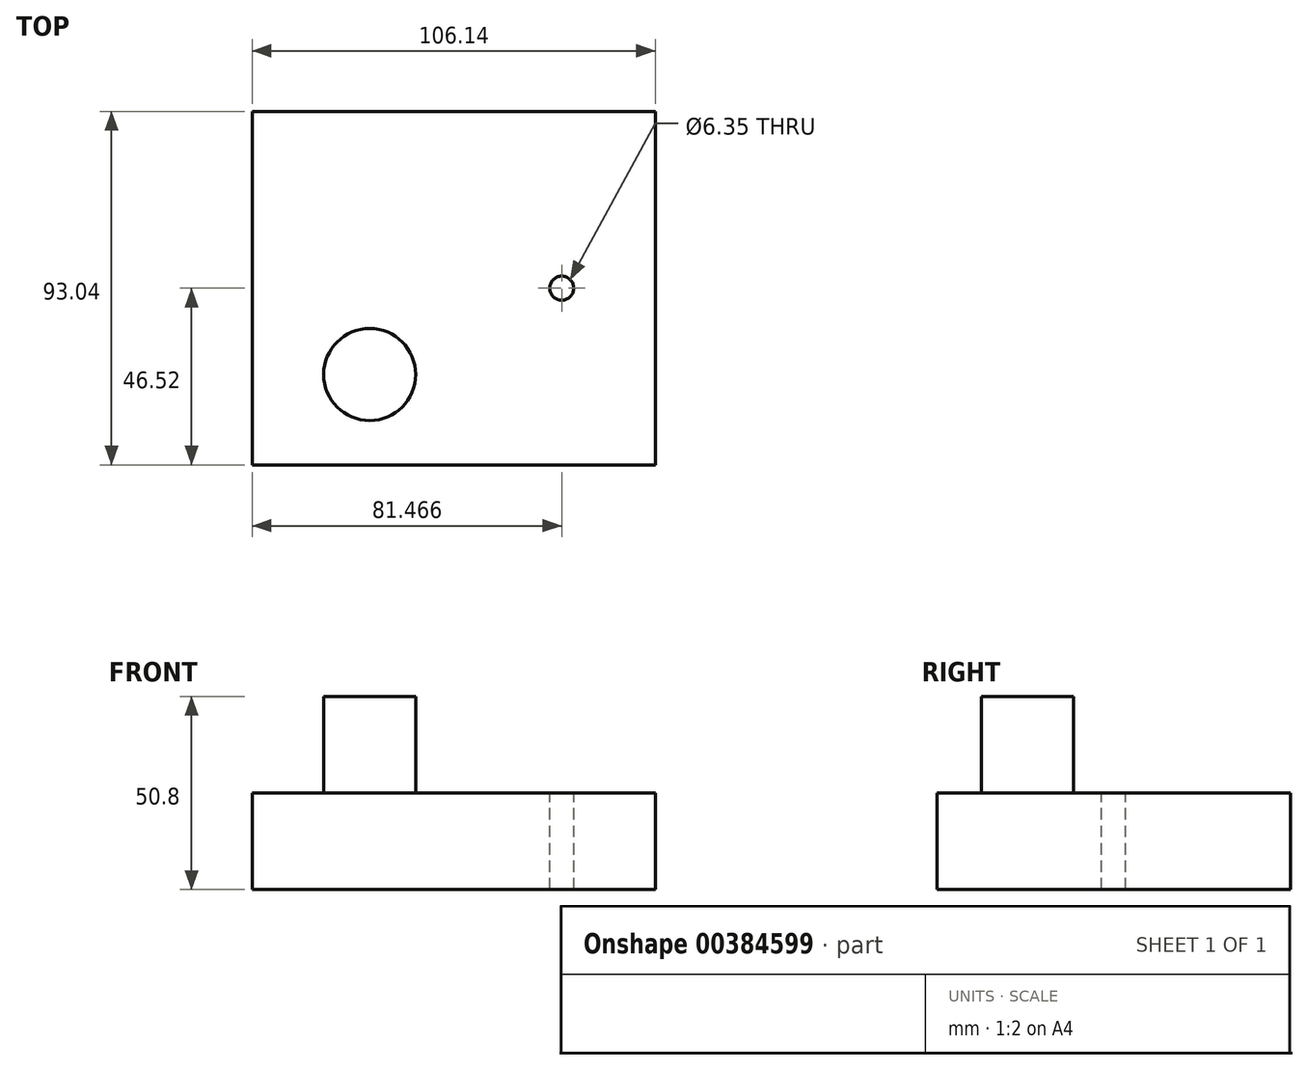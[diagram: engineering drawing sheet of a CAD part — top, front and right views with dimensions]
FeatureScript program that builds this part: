
annotation { "Feature Type Name" : "Feature", "Feature Type Description" : "" }
export const myFeature = defineFeature(function(context is Context, id is Id, definition is map)
    precondition{}
    {
        {
            var Q0;
            Q0=qCreatedBy(makeId("Top.planeOp"),FACE);
            var sketch = newSketch(context, id + "F0", { "sketchPlane" : qUnion([Q0])});
            skLineSegment(sketch, "E0.bottom", {"start": v(-53.07, 46.52) * mm, "end": v(53.07, 46.52) * mm});
            skLineSegment(sketch, "E0.top", {"start": v(-53.07, -46.52) * mm, "end": v(53.07, -46.52) * mm});
            skLineSegment(sketch, "E0.left", {"start": v(-53.07, 46.52) * mm, "end": v(-53.07, -46.52) * mm});
            skLineSegment(sketch, "E0.right", {"start": v(53.07, 46.52) * mm, "end": v(53.07, -46.52) * mm});
            skPoint(sketch, "E0.middle", {"position": v(0, 0) * mm});
            skSolve(sketch);
        }
        {
            var Q0;
            Q0=makeQuery(id+"F0.imprint","IMPRINT",FACE,{"disambiguationData":[TD([[makeQuery(id+"F0.imprint","IMPRINT",EDGE,{"derivedFrom":sQuery(id+"F0.wireOp",EDGE,"E0.bottom")}),-1.0]])]});
            extrude(context, id + "F1", {"entities" : qUnion([Q0]), "depth" : 25.4 * mm});
        }
        {
            var Q0;
            Q0=makeQuery(id+"F1.opExtrude","CAP_FACE",FACE,{"disambiguationData":[OSD([sQuery(id+"F0.wireOp",EDGE,"E0.bottom"),sQuery(id+"F0.wireOp",EDGE,"E0.top"),sQuery(id+"F0.wireOp",EDGE,"E0.left"),sQuery(id+"F0.wireOp",EDGE,"E0.right")])],"isStart":false});
            var sketch = newSketch(context, id + "F2", { "sketchPlane" : qUnion([Q0])});
            skPoint(sketch, "E1", {"position": v(28.4, 0) * mm});
            skSolve(sketch);
        }
        {
            var Q0;
            Q0=sQuery(id+"F2.wireOp",VERTEX,"E1");
            var Q1;
            Q1=makeQuery(id+"F1.opExtrude","SWEPT_BODY",BODY,{"disambiguationData":[OSD([sQuery(id+"F0.wireOp",EDGE,"E0.bottom"),sQuery(id+"F0.wireOp",EDGE,"E0.top"),sQuery(id+"F0.wireOp",EDGE,"E0.left"),sQuery(id+"F0.wireOp",EDGE,"E0.right")])]});
            hole(context, id + "F3", {"style" : HoleStyle.SIMPLE, "endStyle" : HoleEndStyle.THROUGH, "holeDiameter" : 6.35 * mm, "isTappedThrough" : true, "tappedDepth" : 12.7 * mm, "tapClearance" : 3, "locations" : qUnion([Q0]), "scope" : qUnion([Q1])});
        }
        {
            var Q0;
            Q0=makeQuery(id+"F1.opExtrude","CAP_FACE",FACE,{"disambiguationData":[OSD([sQuery(id+"F0.wireOp",EDGE,"E0.bottom"),sQuery(id+"F0.wireOp",EDGE,"E0.top"),sQuery(id+"F0.wireOp",EDGE,"E0.left"),sQuery(id+"F0.wireOp",EDGE,"E0.right")])],"isStart":false});
            var sketch = newSketch(context, id + "F4", { "sketchPlane" : qUnion([Q0])});
            skCircle(sketch, "E2", {"center": v(-22.17, -22.71) * mm, "radius": 12.12 * mm});
            skSolve(sketch);
        }
        {
            var Q0;
            Q0=makeQuery(id+"F4.imprint","IMPRINT",FACE,{"disambiguationData":[TD([[makeQuery(id+"F4.imprint","IMPRINT",EDGE,{"derivedFrom":sQuery(id+"F4.wireOp",EDGE,"E2")}),1.0]])]});
            extrude(context, id + "F5", {"entities" : qUnion([Q0]), "operationType" : NewBodyOperationType.ADD, "depth" : 25.4 * mm});
        }
    });
